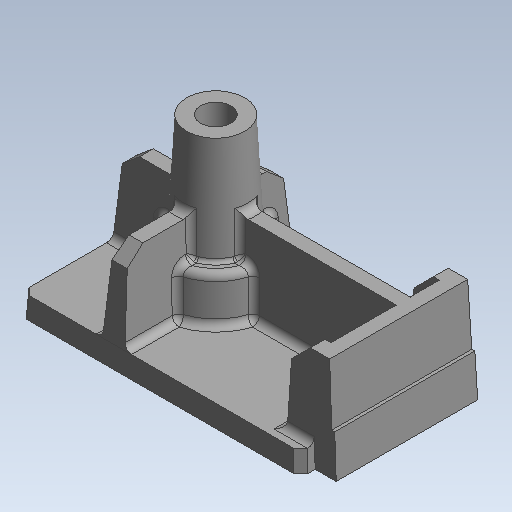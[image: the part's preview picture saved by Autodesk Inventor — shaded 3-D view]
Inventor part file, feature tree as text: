
AUTODESK INVENTOR PART (.ipt)
format: ipt  version: 2020 (Build 240168000, 168)  size: 417,280 bytes
history: native  units: mm (DEFAULTED — no unit token found)
features: fillet x1
ambient origin geometry x8: Origin, YZ Plane, XZ Plane, XY Plane, X Axis, Y Axis, Z Axis, Center Point
bodies: Solid1 (feature_tree)
feature tree (1):
  fillet  "Fillet10"  [1 undecoded]
note: 1 required parameter value undecoded (feature->parameter linkage not recoverable at this tier; creation-order binding heuristic only, values carry confidence <= 0.55)
